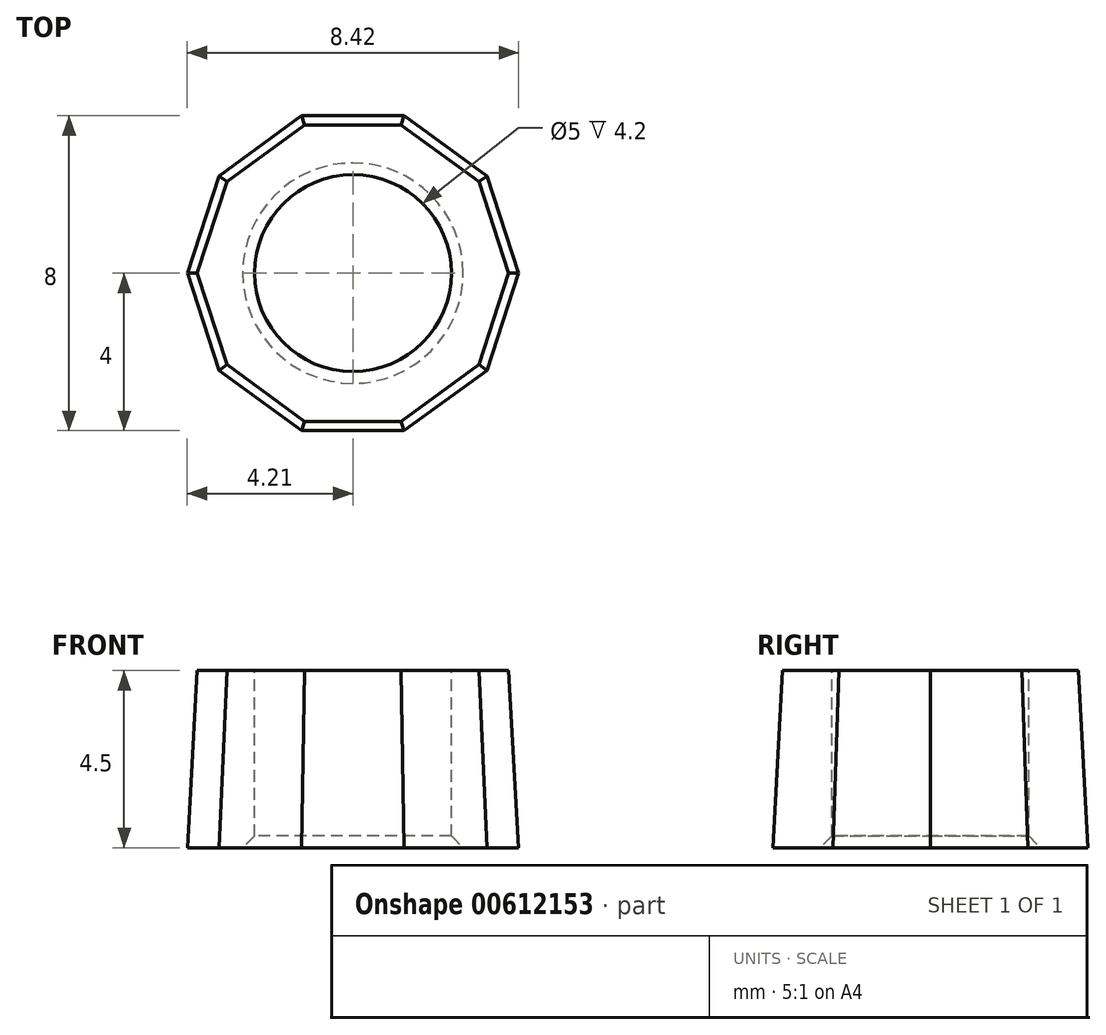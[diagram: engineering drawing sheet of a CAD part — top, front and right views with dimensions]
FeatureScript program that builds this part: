
annotation { "Feature Type Name" : "Feature", "Feature Type Description" : "" }
export const myFeature = defineFeature(function(context is Context, id is Id, definition is map)
    precondition{}
    {
        {
            var Q0;
            Q0=qCreatedBy(makeId("Top.planeOp"),FACE);
            var sketch = newSketch(context, id + "F0", { "sketchPlane" : qUnion([Q0])});
            skCircle(sketch, "E0.cCircle", {"center": v(0, 0) * mm, "radius": 4 * mm, "construction": true});
            skLineSegment(sketch, "E0.0", {"start": v(1.3, -4) * mm, "end": v(-1.3, -4) * mm});
            skLineSegment(sketch, "E0.1", {"start": v(-1.3, -4) * mm, "end": v(-3.4, -2.47) * mm});
            skLineSegment(sketch, "E0.2", {"start": v(-3.4, -2.47) * mm, "end": v(-4.2, 0) * mm});
            skLineSegment(sketch, "E0.3", {"start": v(-4.2, 0) * mm, "end": v(-3.4, 2.47) * mm});
            skLineSegment(sketch, "E0.4", {"start": v(-3.4, 2.47) * mm, "end": v(-1.3, 4) * mm});
            skLineSegment(sketch, "E0.5", {"start": v(-1.3, 4) * mm, "end": v(1.3, 4) * mm});
            skLineSegment(sketch, "E0.6", {"start": v(1.3, 4) * mm, "end": v(3.4, 2.47) * mm});
            skLineSegment(sketch, "E0.7", {"start": v(3.4, 2.47) * mm, "end": v(4.2, 0) * mm});
            skLineSegment(sketch, "E0.8", {"start": v(4.2, 0) * mm, "end": v(3.4, -2.47) * mm});
            skLineSegment(sketch, "E0.9", {"start": v(3.4, -2.47) * mm, "end": v(1.3, -4) * mm});
            skPoint(sketch, "E0.0.midPoint", {"position": v(0, -4) * mm});
            skSolve(sketch);
        }
        {
            var Q0;
            Q0=makeQuery(id+"F0.imprint","IMPRINT",FACE,{"disambiguationData":[TD([[makeQuery(id+"F0.imprint","IMPRINT",EDGE,{"derivedFrom":sQuery(id+"F0.wireOp",EDGE,"E0.0")}),-1.0]])]});
            extrude(context, id + "F1", {"entities" : qUnion([Q0]), "depth" : 4.5 * mm, "offsetDistance" : 25 * mm, "hasDraft" : true, "draftAngle" : 3 * degree, "draftPullDirection" : true});
        }
        {
            var Q0;
            Q0=makeQuery(id+"F1.opExtrude","CAP_FACE",FACE,{"disambiguationData":[OSD([sQuery(id+"F0.wireOp",EDGE,"E0.0"),sQuery(id+"F0.wireOp",EDGE,"E0.1"),sQuery(id+"F0.wireOp",EDGE,"E0.2"),sQuery(id+"F0.wireOp",EDGE,"E0.3"),sQuery(id+"F0.wireOp",EDGE,"E0.4"),sQuery(id+"F0.wireOp",EDGE,"E0.5"),sQuery(id+"F0.wireOp",EDGE,"E0.6"),sQuery(id+"F0.wireOp",EDGE,"E0.7"),sQuery(id+"F0.wireOp",EDGE,"E0.8"),sQuery(id+"F0.wireOp",EDGE,"E0.9")])],"isStart":false});
            var sketch = newSketch(context, id + "F2", { "sketchPlane" : qUnion([Q0])});
            skCircle(sketch, "E1", {"center": v(0, 0) * mm, "radius": 2.5 * mm});
            skSolve(sketch);
        }
        {
            var Q0;
            Q0=makeQuery(id+"F2.imprint","IMPRINT",FACE,{"disambiguationData":[TD([[makeQuery(id+"F2.imprint","IMPRINT",EDGE,{"derivedFrom":sQuery(id+"F2.wireOp",EDGE,"E1")}),1.0]])]});
            extrude(context, id + "F3", {"entities" : qUnion([Q0]), "operationType" : NewBodyOperationType.REMOVE, "oppositeDirection" : true, "depth" : 25 * mm, "offsetDistance" : 25 * mm});
        }
        {
            var Q0;
            Q0=makeQuery(id+"F3.boolean.opBoolean","COPY",EDGE,{"derivedFrom":makeQuery(id+"F3.opExtrude","CAP_EDGE",EDGE,{"disambiguationData":[OSD([sQuery(id+"F2.wireOp",EDGE,"E1")])],"isStart":true})});
            var Q1;
            Q1=makeQuery(id+"F3.boolean.opBoolean","INTERSECT",EDGE,{"derivedFrom":[makeQuery(id+"F1.opExtrude","CAP_FACE",FACE,{"disambiguationData":[OSD([sQuery(id+"F0.wireOp",EDGE,"E0.0"),sQuery(id+"F0.wireOp",EDGE,"E0.1"),sQuery(id+"F0.wireOp",EDGE,"E0.2"),sQuery(id+"F0.wireOp",EDGE,"E0.3"),sQuery(id+"F0.wireOp",EDGE,"E0.4"),sQuery(id+"F0.wireOp",EDGE,"E0.5"),sQuery(id+"F0.wireOp",EDGE,"E0.6"),sQuery(id+"F0.wireOp",EDGE,"E0.7"),sQuery(id+"F0.wireOp",EDGE,"E0.8"),sQuery(id+"F0.wireOp",EDGE,"E0.9")])],"isStart":true}),makeQuery(id+"F3.opExtrude","SWEPT_FACE",FACE,{"disambiguationData":[OSD([sQuery(id+"F2.wireOp",EDGE,"E1")])]})]});
            chamfer(context, id + "F4", {"entities" : qUnion([Q0, Q1]), "width" : 0.3 * mm, "tangentPropagation" : true});
        }
    });
